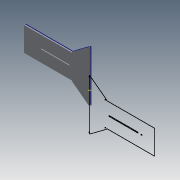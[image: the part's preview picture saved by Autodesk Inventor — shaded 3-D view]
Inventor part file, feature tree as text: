
AUTODESK INVENTOR PART (.ipt)
format: ipt  version: 2015 (Build 190159000, 159)  size: 151,552 bytes
history: native  units: mm
features: other x6, sketch x2, extrude x1, projected_geometry x1
ambient origin geometry x8: Origin, YZ Plane, XZ Plane, XY Plane, X Axis, Y Axis, Z Axis, Center Point
bodies: Body1 (feature_tree)
feature tree (10):
  other  "Blocks"
  extrude  "Extrusion2"  Depth=810.0mm
  sketch  "Sketch5"  dims[d27=30.0mm d28=150.0mm d29=150.0mm d30=30.0mm d31=30.0mm d32=200.0mm d33=200.0mm d35=10.0mm d36=10.0mm d39=50.0mm d40=20.0mm d41=0.0mm d42=300.0mm d43=300.0mm d44=150.0mm d46=10.0mm d47=150.0mm d48=250.0mm d49=350.0mm d50=0.22mm]
  other  "DXF"
  sketch  "Sketch1"  dims[d25=810.0mm d26=30.0mm]
  other  "Block1"
  projected_geometry  "Projected Loop3"
  other  "Block2"
  other  "Block2:1"
  other  "Block2:2"
